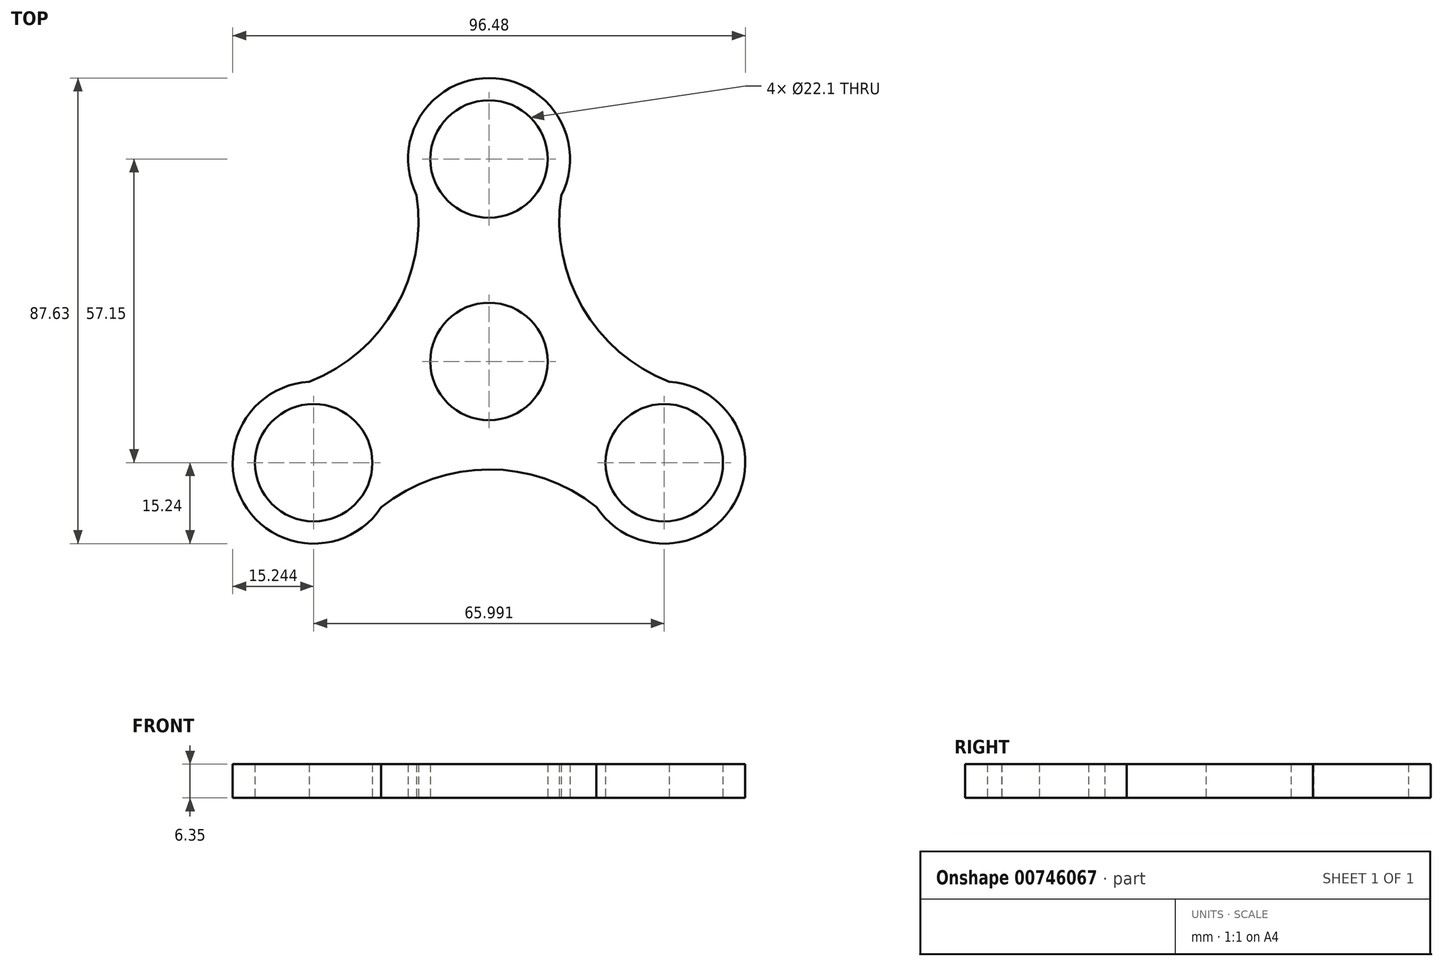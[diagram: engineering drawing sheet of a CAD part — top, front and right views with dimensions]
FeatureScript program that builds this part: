
annotation { "Feature Type Name" : "Feature", "Feature Type Description" : "" }
export const myFeature = defineFeature(function(context is Context, id is Id, definition is map)
    precondition{}
    {
        {
            var Q0;
            Q0=qCreatedBy(makeId("Top.planeOp"),FACE);
            var sketch = newSketch(context, id + "F0", { "sketchPlane" : qUnion([Q0])});
            skCircle(sketch, "E0", {"center": v(0, 0) * mm, "radius": 11.05 * mm});
            skCircle(sketch, "E1", {"center": v(0, 38.1) * mm, "radius": 11.05 * mm});
            skArc(sketch, "E2", {"start": v(13.6, 31.2) * mm, "mid": v(0.05, 53.34) * mm, "end": v(-13.64, 31.3) * mm});
            skCircle(sketch, "E3.1.0", {"center": v(-33, -19.05) * mm, "radius": 11.05 * mm});
            skArc(sketch, "E3.1.1", {"start": v(-33.82, -3.83) * mm, "mid": v(-46.22, -26.63) * mm, "end": v(-20.28, -27.46) * mm});
            skCircle(sketch, "E3.2.0", {"center": v(33, -19.05) * mm, "radius": 11.05 * mm});
            skArc(sketch, "E3.2.1", {"start": v(20.23, -27.38) * mm, "mid": v(46.17, -26.71) * mm, "end": v(33.92, -3.84) * mm});
            skArc(sketch, "E4", {"start": v(-33.82, -3.83) * mm, "mid": v(-17.57, 10.2) * mm, "end": v(-13.64, 31.3) * mm});
            skArc(sketch, "E5.1.0", {"start": v(20.23, -27.38) * mm, "mid": v(-0.04, -20.32) * mm, "end": v(-20.28, -27.46) * mm});
            skArc(sketch, "E5.2.0", {"start": v(13.6, 31.2) * mm, "mid": v(17.61, 10.12) * mm, "end": v(33.92, -3.84) * mm});
            skSolve(sketch);
        }
        {
            var Q0;
            Q0 = qSketchRegion(id + "F0", true);
            extrude(context, id + "F1", {"entities" : qUnion([Q0]), "depth" : 6.35 * mm, "offsetDistance" : 25.4 * mm});
        }
    });
